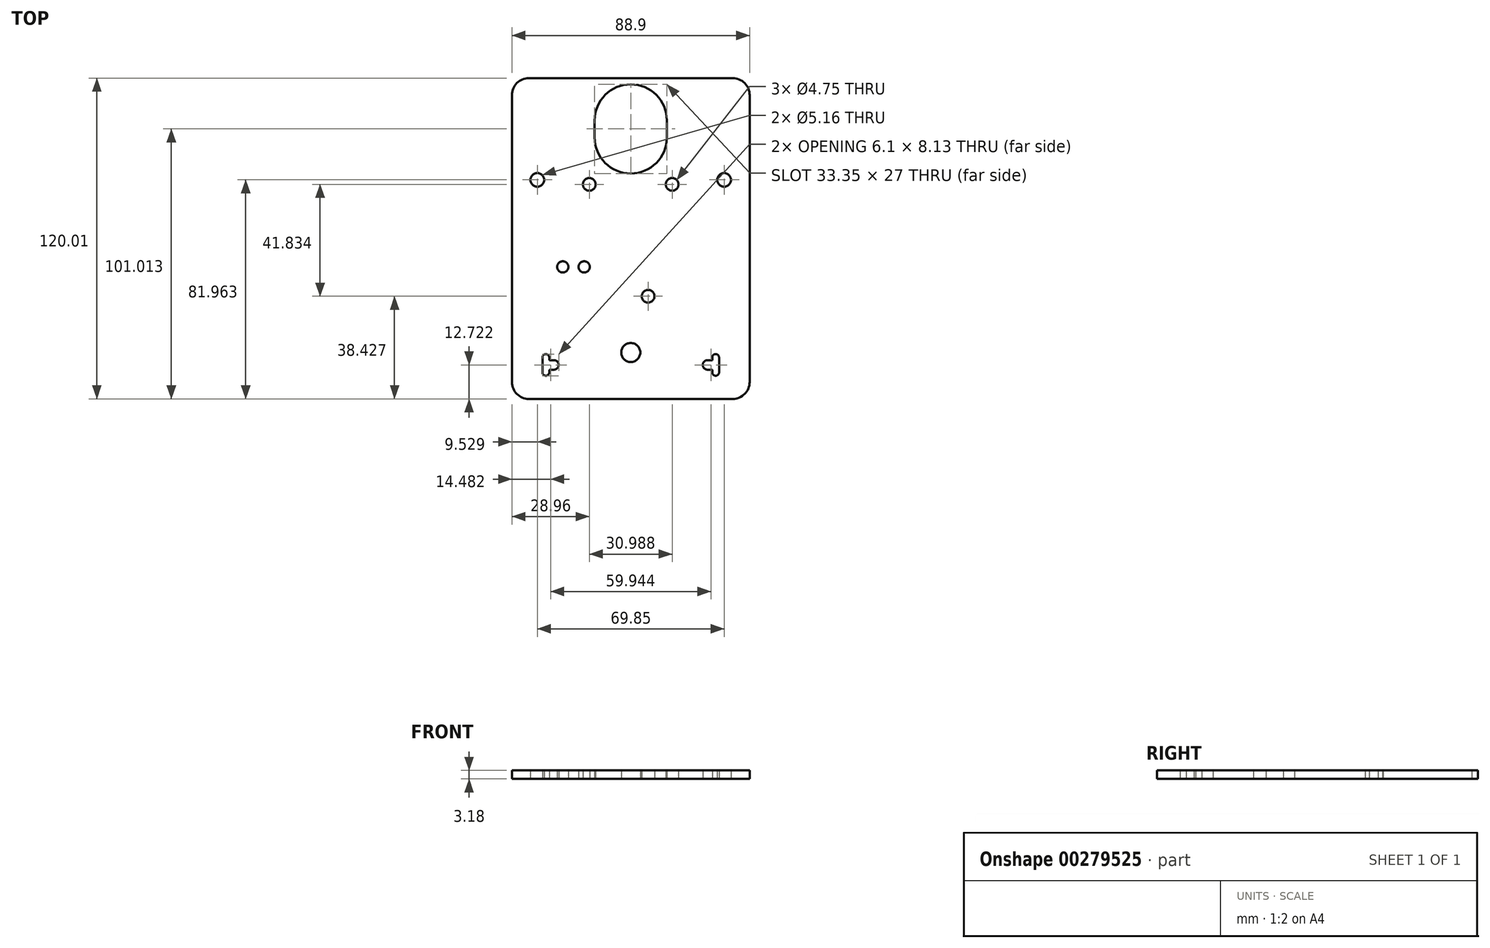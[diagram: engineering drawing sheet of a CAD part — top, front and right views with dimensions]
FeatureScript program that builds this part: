
annotation { "Feature Type Name" : "Feature", "Feature Type Description" : "" }
export const myFeature = defineFeature(function(context is Context, id is Id, definition is map)
    precondition{}
    {
        {
            var Q0;
            Q0=qCreatedBy(makeId("Top.planeOp"),FACE);
            var sketch = newSketch(context, id + "F0", { "sketchPlane" : qUnion([Q0])});
            skLineSegment(sketch, "E0.bottom", {"start": v(-32.69, 70.61) * mm, "end": v(43.51, 70.61) * mm});
            skLineSegment(sketch, "E0.top", {"start": v(-32.69, -49.4) * mm, "end": v(43.51, -49.4) * mm});
            skLineSegment(sketch, "E0.left", {"start": v(-39.04, 64.26) * mm, "end": v(-39.04, -43.05) * mm});
            skLineSegment(sketch, "E0.right", {"start": v(49.86, 64.26) * mm, "end": v(49.86, -43.05) * mm});
            skArc(sketch, "E1.filletArc", {"start": v(-32.69, 70.61) * mm, "mid": v(-37.18, 68.75) * mm, "end": v(-39.04, 64.26) * mm});
            skArc(sketch, "E2.filletArc", {"start": v(49.86, 64.26) * mm, "mid": v(48, 68.75) * mm, "end": v(43.51, 70.61) * mm});
            skArc(sketch, "E3.filletArc", {"start": v(-39.04, -43.05) * mm, "mid": v(-37.18, -47.54) * mm, "end": v(-32.69, -49.4) * mm});
            skArc(sketch, "E4.filletArc", {"start": v(43.51, -49.4) * mm, "mid": v(48, -47.54) * mm, "end": v(49.86, -43.05) * mm});
            skCircle(sketch, "E5", {"center": v(-29.51, 32.56) * mm, "radius": 2.58 * mm});
            skCircle(sketch, "E6.MirrorC", {"center": v(40.34, 32.56) * mm, "radius": 2.58 * mm});
            skCircle(sketch, "E7", {"center": v(-10.08, 30.86) * mm, "radius": 2.37 * mm});
            skCircle(sketch, "E8.MirrorC", {"center": v(20.9, 30.86) * mm, "radius": 2.37 * mm});
            skCircle(sketch, "E9", {"center": v(-19.99, 0) * mm, "radius": 2.1 * mm});
            skCircle(sketch, "E10", {"center": v(-11.99, 0) * mm, "radius": 2.1 * mm});
            skCircle(sketch, "E11", {"center": v(11.92, -10.97) * mm, "radius": 2.37 * mm});
            skLineSegment(sketch, "E12", {"start": v(-26.34, -32.61) * mm, "end": v(-26.34, -32.61) * mm});
            skLineSegment(sketch, "E13", {"start": v(-25.07, -33.88) * mm, "end": v(-25.07, -34.9) * mm});
            skLineSegment(sketch, "E14", {"start": v(-25.07, -34.9) * mm, "end": v(-23.29, -34.9) * mm});
            skLineSegment(sketch, "E15", {"start": v(-21.51, -36.68) * mm, "end": v(-21.51, -36.68) * mm});
            skLineSegment(sketch, "E16", {"start": v(-23.29, -38.46) * mm, "end": v(-25.07, -38.46) * mm});
            skLineSegment(sketch, "E17", {"start": v(-25.07, -38.46) * mm, "end": v(-25.07, -39.47) * mm});
            skLineSegment(sketch, "E18", {"start": v(-26.34, -40.74) * mm, "end": v(-26.34, -40.74) * mm});
            skLineSegment(sketch, "E19", {"start": v(-27.6, -33.88) * mm, "end": v(-27.6, -39.47) * mm});
            skArc(sketch, "E20.filletArc", {"start": v(-21.51, -36.68) * mm, "mid": v(-22.03, -35.42) * mm, "end": v(-23.29, -34.9) * mm});
            skArc(sketch, "E21.filletArc", {"start": v(-23.29, -38.46) * mm, "mid": v(-22.03, -37.93) * mm, "end": v(-21.51, -36.68) * mm});
            skArc(sketch, "E22.filletArc", {"start": v(-25.07, -33.88) * mm, "mid": v(-25.44, -32.99) * mm, "end": v(-26.34, -32.61) * mm});
            skArc(sketch, "E23.filletArc", {"start": v(-26.34, -32.61) * mm, "mid": v(-27.23, -32.99) * mm, "end": v(-27.6, -33.88) * mm});
            skArc(sketch, "E24.filletArc", {"start": v(-27.6, -39.47) * mm, "mid": v(-27.23, -40.37) * mm, "end": v(-26.34, -40.74) * mm});
            skArc(sketch, "E25.filletArc", {"start": v(-26.34, -40.74) * mm, "mid": v(-25.44, -40.37) * mm, "end": v(-25.07, -39.47) * mm});
            skArc(sketch, "E26.MirrorCS", {"start": v(35.9, -33.88) * mm, "mid": v(36.27, -32.99) * mm, "end": v(37.16, -32.61) * mm});
            skArc(sketch, "E27.MirrorCS", {"start": v(38.43, -39.47) * mm, "mid": v(38.06, -40.37) * mm, "end": v(37.16, -40.74) * mm});
            skArc(sketch, "E28.MirrorCS", {"start": v(37.16, -32.61) * mm, "mid": v(38.06, -32.99) * mm, "end": v(38.43, -33.88) * mm});
            skLineSegment(sketch, "E29.MirrorCS", {"start": v(35.9, -38.46) * mm, "end": v(35.9, -39.47) * mm});
            skArc(sketch, "E30.MirrorCS", {"start": v(37.16, -40.74) * mm, "mid": v(36.27, -40.37) * mm, "end": v(35.9, -39.47) * mm});
            skLineSegment(sketch, "E31.MirrorCS", {"start": v(35.9, -33.88) * mm, "end": v(35.9, -34.9) * mm});
            skLineSegment(sketch, "E32.MirrorCS", {"start": v(34.12, -38.46) * mm, "end": v(35.9, -38.46) * mm});
            skLineSegment(sketch, "E33.MirrorCS", {"start": v(35.9, -34.9) * mm, "end": v(34.12, -34.9) * mm});
            skArc(sketch, "E34.MirrorCS", {"start": v(34.12, -38.46) * mm, "mid": v(32.86, -37.93) * mm, "end": v(32.34, -36.68) * mm});
            skArc(sketch, "E35.MirrorCS", {"start": v(32.34, -36.68) * mm, "mid": v(32.86, -35.42) * mm, "end": v(34.12, -34.9) * mm});
            skLineSegment(sketch, "E36.MirrorCS", {"start": v(38.43, -33.88) * mm, "end": v(38.43, -39.47) * mm});
            skLineSegment(sketch, "E37.MirrorCS", {"start": v(32.34, -36.68) * mm, "end": v(32.34, -36.68) * mm});
            skLineSegment(sketch, "E38.MirrorCS", {"start": v(37.16, -40.74) * mm, "end": v(37.16, -40.74) * mm});
            skLineSegment(sketch, "E39.MirrorCS", {"start": v(37.16, -32.61) * mm, "end": v(37.16, -32.61) * mm});
            skCircle(sketch, "E40", {"center": v(5.41, -32.03) * mm, "radius": 3.57 * mm});
            skLineSegment(sketch, "E41.bottom", {"start": v(5.41, 68.29) * mm, "end": v(5.41, 68.29) * mm});
            skLineSegment(sketch, "E41.top", {"start": v(5.41, 34.94) * mm, "end": v(5.41, 34.94) * mm});
            skLineSegment(sketch, "E41.left", {"start": v(-8.09, 54.79) * mm, "end": v(-8.09, 48.44) * mm});
            skLineSegment(sketch, "E41.right", {"start": v(18.91, 54.79) * mm, "end": v(18.91, 48.44) * mm});
            skArc(sketch, "E42.filletArc", {"start": v(-8.09, 48.44) * mm, "mid": v(-4.13, 38.9) * mm, "end": v(5.41, 34.94) * mm});
            skArc(sketch, "E43.filletArc", {"start": v(5.41, 34.94) * mm, "mid": v(14.96, 38.9) * mm, "end": v(18.91, 48.44) * mm});
            skArc(sketch, "E44.filletArc", {"start": v(18.91, 54.79) * mm, "mid": v(14.96, 64.33) * mm, "end": v(5.41, 68.29) * mm});
            skArc(sketch, "E45.filletArc", {"start": v(5.41, 68.29) * mm, "mid": v(-4.13, 64.33) * mm, "end": v(-8.09, 54.79) * mm});
            skLineSegment(sketch, "E46", {"start": v(5.41, 68.29) * mm, "end": v(5.41, 34.94) * mm});
            skLineSegment(sketch, "E47", {"start": v(18.91, 51.61) * mm, "end": v(5.41, 51.61) * mm});
            skSolve(sketch);
        }
        {
            var Q0;
            Q0 = qSketchRegion(id + "F0", true);
            extrude(context, id + "F1", {"entities" : qUnion([Q0]), "depth" : 3.17 * mm});
        }
    });
